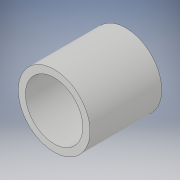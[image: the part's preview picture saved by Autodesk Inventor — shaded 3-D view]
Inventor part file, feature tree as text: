
AUTODESK INVENTOR PART (.ipt)
format: ipt  version: 2019 (Build 230136000, 136)  size: 100,864 bytes
history: native  units: mm
features: extrude x2, sketch x2
ambient origin geometry x8: Origin, YZ Plane, XZ Plane, XY Plane, X Axis, Y Axis, Z Axis, Center Point
bodies: Solid1 (feature_tree)
feature tree (4):
  extrude  "Extrusion1"  Depth=250.0mm TaperAngle=0.0deg
  extrude  "Extrusion2"  Depth=21.5mm TaperAngle=0.0deg
  sketch  "Sketch1"  dims[d0=250.0mm d1=250.0mm d2=0.0mm]
  sketch  "Sketch2"  dims[d3=200.0mm d4=21.5mm d5=0.0mm]
